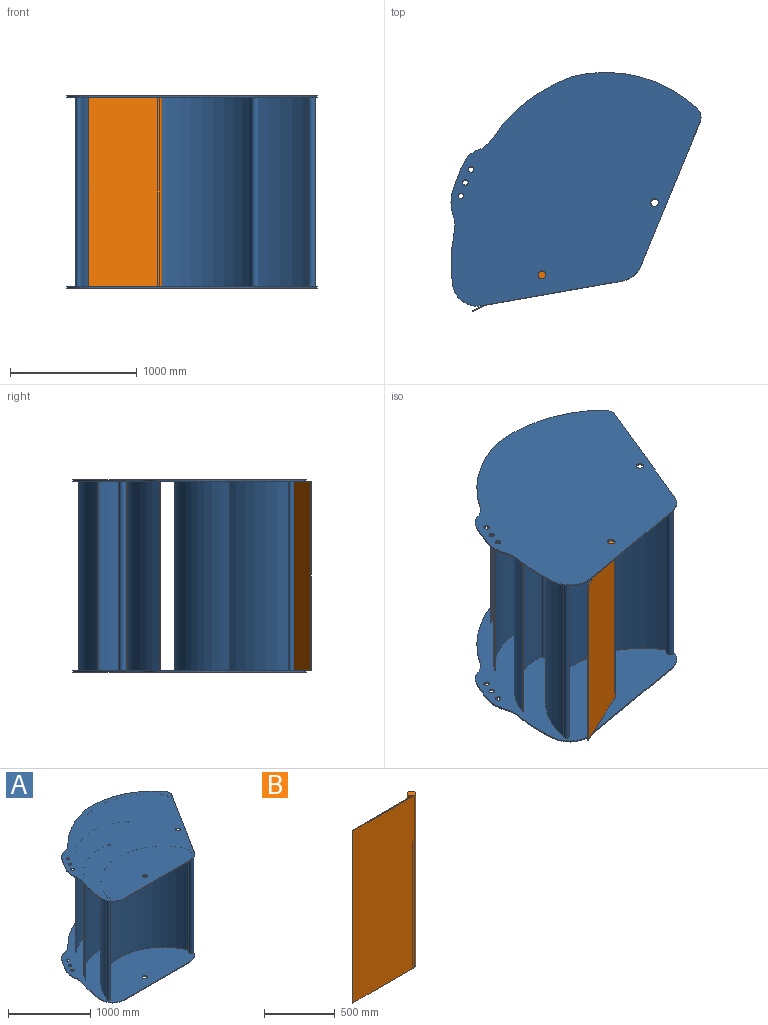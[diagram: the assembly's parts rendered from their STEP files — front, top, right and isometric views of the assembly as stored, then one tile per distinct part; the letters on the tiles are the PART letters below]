
ASSEMBLY  parts=2 mates=2
PART A: 61 faces, bbox 2164.2x1661x1520 mm
  f0: cylinder r=30.5mm len=61mm, axis (0,0,-1), area 1916.4mm2, adj f48,f49
  f1: cylinder r=29.5mm len=59mm, axis (0,0,-1), area 1853.5mm2, adj f48,f49
  f2: cylinder r=22mm len=44mm, axis (0,0,-1), area 1382.3mm2, adj f48,f49
  f3: cylinder r=22mm len=44mm, axis (0,0,-1), area 1382.3mm2, adj f48,f49
  f4: cylinder r=22mm len=44mm, axis (0,0,-1), area 1382.3mm2, adj f48,f49
  f5: cylinder r=326.18mm len=176.61mm, axis (0,0,-1), area 1797.7mm2, adj f48,f49,f50,f60
  f6: cylinder r=200mm len=212.82mm, axis (0,0,-1), area 3269.9mm2, adj f48,f49,f51,f52
  f7: cylinder r=20.5mm len=1500mm, axis (0,0,-1), area 183146.8mm2, adj f30,f44,f45,f49
  f8: cylinder r=30.5mm len=1500mm, axis (0,0,-1), area 272705.4mm2, adj f30,f44,f45,f46,f47,f49
  f9: cylinder r=15.5mm len=1500mm, axis (0,0,-1), area 135747.8mm2, adj f30,f41,f43,f49
  f10: cylinder r=15.5mm len=1500mm, axis (0,0,-1), area 136340.4mm2, adj f30,f37,f40,f49
  f11: cylinder r=30.5mm len=1500mm, axis (0,0,-1), area 274743.1mm2, adj f30,f32,f34,f35,f36,f49
  f12: cylinder r=30.5mm len=61mm, axis (0,0,-1), area 1916.4mm2, adj f30,f31
  f13: cylinder r=22mm len=44mm, axis (0,0,-1), area 1382.3mm2, adj f30,f31
  f14: cylinder r=22mm len=44mm, axis (0,0,-1), area 1382.3mm2, adj f30,f31
  f15: cylinder r=22mm len=44mm, axis (0,0,-1), area 1382.3mm2, adj f30,f31
  f16: cylinder r=29.5mm len=59mm, axis (0,0,-1), area 1853.5mm2, adj f30,f31
  f17: cylinder r=326.18mm len=176.61mm, axis (0,0,-1), area 1797.7mm2, adj f28,f29,f30,f31
  f18: cylinder r=200mm len=212.82mm, axis (0,0,-1), area 3269.9mm2, adj f19,f20,f30,f31
  f19: cylinder r=1403.06mm len=415.74mm, axis (0,0,-1), area 4273.2mm2, adj f18,f29,f30,f31
  f20: plane 1123.76x10mm, normal (0,-1,0), area 11237.6mm2, adj f18,f21,f30,f31
  f21: cylinder r=200mm len=169mm, axis (0,0,-1), area 2013.2mm2, adj f20,f22,f30,f31
  f22: plane 1036.5x655.9mm, normal (0.85,-0.53,0), area 12265.9mm2, adj f21,f23,f30,f31,f36,f47
  f23: cylinder r=100mm len=114.68mm, axis (0,0,-1), area 1222.9mm2, adj f22,f24,f30,f31
  f24: cylinder r=1074.34mm len=926.41mm, axis (0,0,-1), area 10568mm2, adj f23,f25,f30,f31
  f25: cylinder r=1282.61mm len=713.26mm, axis (0,0,-1), area 8227.7mm2, adj f24,f26,f30,f31
  f26: cylinder r=200mm len=117.51mm, axis (0,0,-1), area 1346.6mm2, adj f25,f27,f30,f31
  f27: cylinder r=186.95mm len=116.81mm, axis (0,0,-1), area 1363.1mm2, adj f26,f28,f30,f31
  f28: cylinder r=1324.47mm len=239.75mm, axis (0,0,-1), area 2828.3mm2, adj f17,f27,f30,f31
  f29: cylinder r=200mm len=107.43mm, axis (0,0,-1), area 1093.1mm2, adj f17,f19,f30,f31
  f30: plane 2164.16x1660.98mm, normal (0,0,1), area 2565292.9mm2, adj f7,f8,f9,f10,f11,f12,f13,f14
  f31: plane 2164.16x1660.98mm, normal (0,0,-1), area 2603609.2mm2, adj f12,f13,f14,f15,f16,f17,f18,f19
  f32: cylinder r=883.17mm len=1500mm, axis (0,0,-1), area 1936048.7mm2, adj f11,f30,f33,f49
  f33: plane 1500x5.5mm, normal (-0.92,-0.4,0), area 9000mm2, adj f30,f32,f34,f49
  f34: cylinder r=877.17mm len=1500mm, axis (0,0,-1), area 1914005.6mm2, adj f11,f30,f33,f49
  f35: plane 9.3x5.88mm, normal (0,0,1), area 3.7mm2, adj f11,f54
  f36: plane 9.3x5.88mm, normal (0,0,-1), area 3.7mm2, adj f11,f22
  f37: cylinder r=685.89mm len=1500mm, axis (0,0,-1), area 1444091.5mm2, adj f10,f30,f38,f49
  f38: plane 1500x4.62mm, normal (-0.77,-0.64,0), area 9000mm2, adj f30,f37,f39,f49
  f39: plane 1500x0.08mm, normal (0.65,-0.76,0), area 152.6mm2, adj f30,f38,f40,f49
  f40: cylinder r=679.89mm len=1500mm, axis (0,0,-1), area 1427930.9mm2, adj f10,f30,f39,f49
  f41: cylinder r=640.37mm len=1500mm, axis (0,0,-1), area 1242581.2mm2, adj f9,f30,f42,f49
  f42: plane 1500x5.24mm, normal (-0.49,-0.87,0), area 9000mm2, adj f30,f41,f43,f49
  f43: cylinder r=634.37mm len=1500mm, axis (0,0,-1), area 1226053.6mm2, adj f9,f30,f42,f49
  f44: cylinder r=755.25mm len=1500mm, axis (0,0,-1), area 2799788.5mm2, adj f7,f8,f30,f49
  f45: cylinder r=761.25mm len=1500mm, axis (0,0,-1), area 2838096.4mm2, adj f7,f8,f30,f49
  f46: plane 9.3x5.88mm, normal (0,0,1), area 3.7mm2, adj f8,f54
  f47: plane 9.3x5.88mm, normal (0,0,-1), area 3.7mm2, adj f8,f22
  f48: plane 2164.16x1660.98mm, normal (0,0,1), area 2603609.2mm2, adj f0,f1,f2,f3,f4,f5,f6,f50
  f49: plane 2164.16x1660.98mm, normal (0,0,-1), area 2565292.9mm2, adj f0,f1,f2,f3,f4,f5,f6,f7
  f50: cylinder r=200mm len=107.43mm, axis (0,0,-1), area 1093.1mm2, adj f5,f48,f49,f51
  f51: cylinder r=1403.06mm len=415.74mm, axis (0,0,-1), area 4273.2mm2, adj f6,f48,f49,f50
  f52: plane 1123.76x10mm, normal (0,-1,0), area 11237.6mm2, adj f6,f48,f49,f53
  f53: cylinder r=200mm len=169mm, axis (0,0,-1), area 2013.2mm2, adj f48,f49,f52,f54
  f54: plane 1036.5x655.9mm, normal (0.85,-0.53,0), area 12265.9mm2, adj f35,f46,f48,f49,f53,f55
  f55: cylinder r=100mm len=114.68mm, axis (0,0,-1), area 1222.9mm2, adj f48,f49,f54,f56
  f56: cylinder r=1074.34mm len=926.41mm, axis (0,0,-1), area 10568mm2, adj f48,f49,f55,f57
  f57: cylinder r=1282.61mm len=713.26mm, axis (0,0,-1), area 8227.7mm2, adj f48,f49,f56,f58
  f58: cylinder r=200mm len=117.51mm, axis (0,0,-1), area 1346.6mm2, adj f48,f49,f57,f59
  f59: cylinder r=186.95mm len=116.81mm, axis (0,0,-1), area 1363.1mm2, adj f48,f49,f58,f60
  f60: cylinder r=1324.47mm len=239.75mm, axis (0,0,-1), area 2828.3mm2, adj f5,f48,f49,f59
PART B: 6 faces, bbox 646.3x61x1490 mm
  f0: cylinder r=30.5mm len=1490mm, axis (0,0,-1), area 256544.7mm2, adj f1,f2,f4,f5
  f1: plane 1490x615.77mm, normal (0,-1,0), area 917501.9mm2, adj f0,f3,f4,f5
  f2: plane 1490x597.61mm, normal (0,1,0), area 890434.7mm2, adj f0,f3,f4,f5
  f3: plane 1490x6mm, normal (-1,0,0), area 8940mm2, adj f1,f2,f4,f5
  f4: plane 646.27x61mm, normal (0,0,1), area 6542.9mm2, adj f0,f1,f2,f3
  f5: plane 646.27x61mm, normal (0,0,-1), area 6542.9mm2, adj f0,f1,f2,f3
PLACE A rot(axis=(0,0,1),10deg) t=(0,0,-10)mm
PLACE B rot(axis=(0,0,1),25deg) t=(-178.07,210.86,-10)mm
MATE planar A.f0 <-> B.f0  axis (0,0,-1) through (-889.87,-570.86,750)mm
MATE revolute A.f0 <-> B.f0  axis (0,0,-1) through (-889.87,-570.86,750)mm
